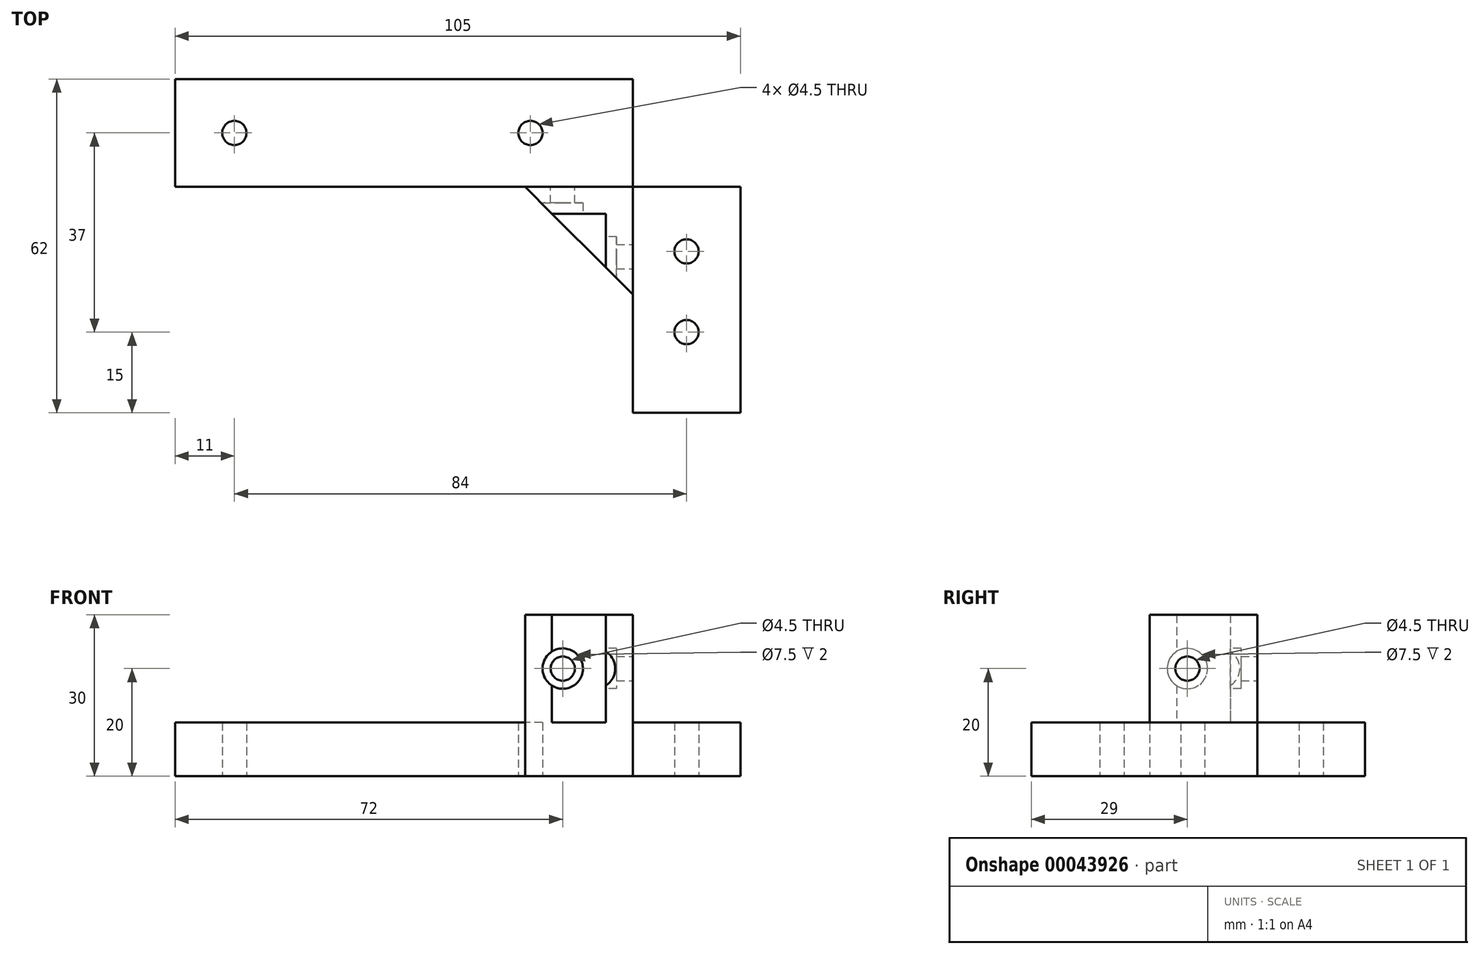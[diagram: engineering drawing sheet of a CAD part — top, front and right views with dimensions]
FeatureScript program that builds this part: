
annotation { "Feature Type Name" : "Feature", "Feature Type Description" : "" }
export const myFeature = defineFeature(function(context is Context, id is Id, definition is map)
    precondition{}
    {
        {
            var Q0;
            Q0=qCreatedBy(makeId("Top.planeOp"),FACE);
            var sketch = newSketch(context, id + "F0", { "sketchPlane" : qUnion([Q0])});
            skLineSegment(sketch, "E0", {"start": v(0, 0) * mm, "end": v(0, -22) * mm});
            skLineSegment(sketch, "E1", {"start": v(0, -22) * mm, "end": v(20, -22) * mm});
            skLineSegment(sketch, "E2", {"start": v(20, -22) * mm, "end": v(20, 20) * mm});
            skLineSegment(sketch, "E3", {"start": v(20, 20) * mm, "end": v(0, 20) * mm});
            skLineSegment(sketch, "E4", {"start": v(0, 20) * mm, "end": v(0, 40) * mm});
            skLineSegment(sketch, "E5", {"start": v(0, 40) * mm, "end": v(-85, 40) * mm});
            skLineSegment(sketch, "E6", {"start": v(-85, 40) * mm, "end": v(-85, 20) * mm});
            skLineSegment(sketch, "E7", {"start": v(-85, 20) * mm, "end": v(-20, 20) * mm});
            skLineSegment(sketch, "E8", {"start": v(-20, 20) * mm, "end": v(0, 0) * mm});
            skLineSegment(sketch, "E9", {"start": v(-19, 40) * mm, "end": v(-19, 30) * mm, "construction": true});
            skCircle(sketch, "E10", {"center": v(-19, 30) * mm, "radius": 2.25 * mm});
            skLineSegment(sketch, "E11", {"start": v(-19, 30) * mm, "end": v(-74, 30) * mm, "construction": true});
            skCircle(sketch, "E12", {"center": v(-74, 30) * mm, "radius": 2.25 * mm});
            skLineSegment(sketch, "E13", {"start": v(10, 20) * mm, "end": v(10, 8) * mm, "construction": true});
            skCircle(sketch, "E14", {"center": v(10, 8) * mm, "radius": 2.25 * mm});
            skLineSegment(sketch, "E15", {"start": v(10, 8) * mm, "end": v(10, -7) * mm, "construction": true});
            skCircle(sketch, "E16", {"center": v(10, -7) * mm, "radius": 2.25 * mm});
            skSolve(sketch);
        }
        {
            var Q0;
            Q0 = qSketchRegion(id + "F0", true);
            extrude(context, id + "F1", {"entities" : qUnion([Q0]), "depth" : 10 * mm});
        }
        {
            var Q0;
            Q0=makeQuery(id+"F1.opExtrude","CAP_FACE",FACE,{"disambiguationData":[OSD([sQuery(id+"F0.wireOp",EDGE,"E0"),sQuery(id+"F0.wireOp",EDGE,"E1"),sQuery(id+"F0.wireOp",EDGE,"E2"),sQuery(id+"F0.wireOp",EDGE,"E3"),sQuery(id+"F0.wireOp",EDGE,"E4"),sQuery(id+"F0.wireOp",EDGE,"E5"),sQuery(id+"F0.wireOp",EDGE,"E6"),sQuery(id+"F0.wireOp",EDGE,"E7"),sQuery(id+"F0.wireOp",EDGE,"E8"),sQuery(id+"F0.wireOp",EDGE,"E10"),sQuery(id+"F0.wireOp",EDGE,"E12"),sQuery(id+"F0.wireOp",EDGE,"E14"),sQuery(id+"F0.wireOp",EDGE,"E16")])],"isStart":false});
            var sketch = newSketch(context, id + "F2", { "sketchPlane" : qUnion([Q0])});
            skLineSegment(sketch, "E17", {"start": v(0, 20) * mm, "end": v(-20, 20) * mm});
            skLineSegment(sketch, "E18", {"start": v(0, 20) * mm, "end": v(0, 0) * mm});
            skLineSegment(sketch, "E19", {"start": v(-10, 15) * mm, "end": v(-5, 15) * mm});
            skLineSegment(sketch, "E20", {"start": v(-5, 15) * mm, "end": v(-5, 10) * mm});
            skLineSegment(sketch, "E21", {"start": v(-5, 10) * mm, "end": v(-5, 5) * mm});
            skLineSegment(sketch, "E22", {"start": v(-5, 5) * mm, "end": v(0, 0) * mm});
            skLineSegment(sketch, "E23", {"start": v(-10, 15) * mm, "end": v(-15, 15) * mm});
            skLineSegment(sketch, "E24", {"start": v(-15, 15) * mm, "end": v(-20, 20) * mm});
            skSolve(sketch);
        }
        {
            var Q0;
            Q0 = qSketchRegion(id + "F2", true);
            extrude(context, id + "F3", {"entities" : qUnion([Q0]), "operationType" : NewBodyOperationType.ADD, "depth" : 20 * mm});
        }
        {
            var Q0;
            Q0=makeQuery(id+"F3.opExtrude","SWEPT_FACE",FACE,{"disambiguationData":[OSD([sQuery(id+"F2.wireOp",EDGE,"E18")])]});
            var sketch = newSketch(context, id + "F4", { "sketchPlane" : qUnion([Q0])});
            skCircle(sketch, "E25", {"center": v(7, 20) * mm, "radius": 2.25 * mm});
            skSolve(sketch);
        }
        {
            var Q0;
            Q0 = qSketchRegion(id + "F4", true);
            extrude(context, id + "F5", {"entities" : qUnion([Q0]), "operationType" : NewBodyOperationType.REMOVE, "oppositeDirection" : true, "depth" : 5 * mm});
        }
        {
            var Q0;
            Q0=makeQuery(id+"F3.opExtrude","SWEPT_FACE",FACE,{"disambiguationData":[OSD([sQuery(id+"F2.wireOp",EDGE,"E17")])]});
            var sketch = newSketch(context, id + "F6", { "sketchPlane" : qUnion([Q0])});
            skCircle(sketch, "E26", {"center": v(13, 20) * mm, "radius": 2.25 * mm});
            skSolve(sketch);
        }
        {
            var Q0;
            Q0=makeQuery(id+"F6.imprint","IMPRINT",FACE,{"disambiguationData":[TD([[makeQuery(id+"F6.imprint","IMPRINT",EDGE,{"derivedFrom":sQuery(id+"F6.wireOp",EDGE,"E26")}),1.0]])]});
            extrude(context, id + "F7", {"entities" : qUnion([Q0]), "operationType" : NewBodyOperationType.REMOVE, "oppositeDirection" : true, "depth" : 10 * mm});
        }
        {
            var Q0;
            Q0=makeQuery(id+"F3.opExtrude","SWEPT_FACE",FACE,{"disambiguationData":[OSD([sQuery(id+"F2.wireOp",EDGE,"E19"),sQuery(id+"F2.wireOp",EDGE,"E23")])]});
            var sketch = newSketch(context, id + "F8", { "sketchPlane" : qUnion([Q0])});
            skCircle(sketch, "E27", {"center": v(-13, 20) * mm, "radius": 3.75 * mm});
            skSolve(sketch);
        }
        {
            var Q0;
            Q0 = qSketchRegion(id + "F8", true);
            extrude(context, id + "F9", {"entities" : qUnion([Q0]), "operationType" : NewBodyOperationType.REMOVE, "oppositeDirection" : true, "depth" : 2 * mm});
        }
        {
            var Q0;
            Q0=makeQuery(id+"F3.opExtrude","SWEPT_FACE",FACE,{"disambiguationData":[OSD([sQuery(id+"F2.wireOp",EDGE,"E20"),sQuery(id+"F2.wireOp",EDGE,"E21")])]});
            var sketch = newSketch(context, id + "F10", { "sketchPlane" : qUnion([Q0])});
            skCircle(sketch, "E28", {"center": v(-7, 20) * mm, "radius": 3.75 * mm});
            skSolve(sketch);
        }
        {
            var Q0;
            Q0 = qSketchRegion(id + "F10", true);
            extrude(context, id + "F11", {"entities" : qUnion([Q0]), "operationType" : NewBodyOperationType.REMOVE, "oppositeDirection" : true, "depth" : 2 * mm});
        }
    });
